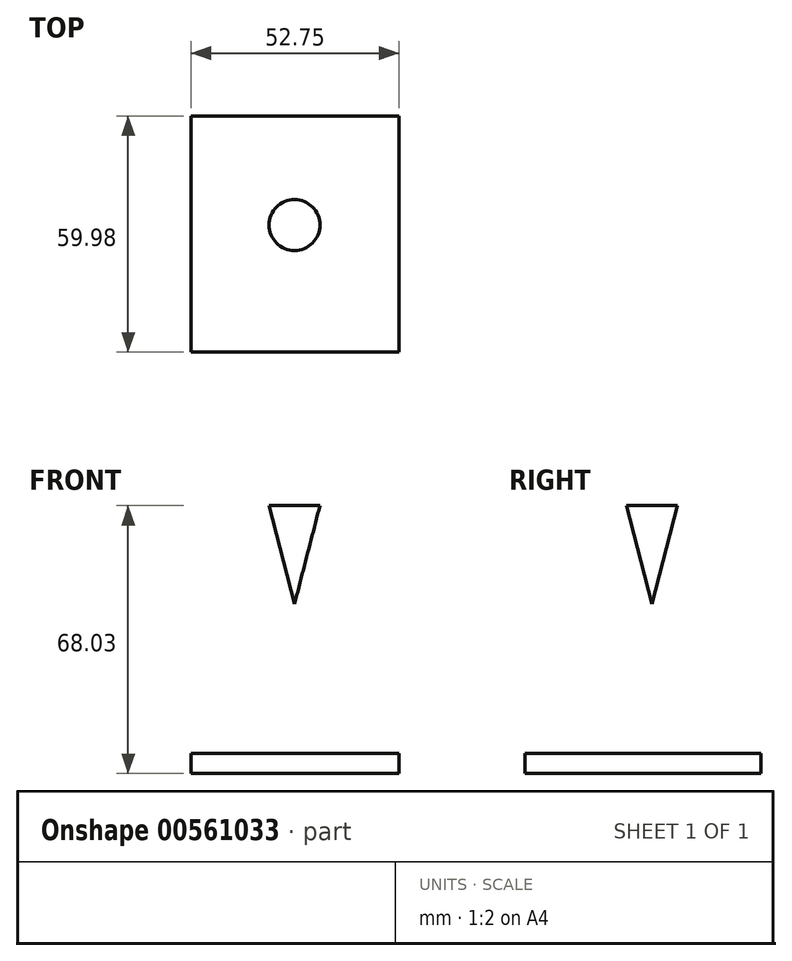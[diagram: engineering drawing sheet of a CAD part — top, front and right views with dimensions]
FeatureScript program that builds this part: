
annotation { "Feature Type Name" : "Feature", "Feature Type Description" : "" }
export const myFeature = defineFeature(function(context is Context, id is Id, definition is map)
    precondition{}
    {
        {
            var Q0;
            Q0=qCreatedBy(makeId("Front.planeOp"),FACE);
            var sketch = newSketch(context, id + "F0", { "sketchPlane" : qUnion([Q0])});
            skLineSegment(sketch, "E0", {"start": v(0, 0) * mm, "end": v(0, 25) * mm});
            skLineSegment(sketch, "E1", {"start": v(0, 25) * mm, "end": v(6.47, 25) * mm});
            skLineSegment(sketch, "E2", {"start": v(6.47, 25) * mm, "end": v(0, 0) * mm});
            skLineSegment(sketch, "E3", {"start": v(0, -37.95) * mm, "end": v(16.47, -37.95) * mm});
            skLineSegment(sketch, "E4", {"start": v(16.47, -37.95) * mm, "end": v(16.47, -42.95) * mm});
            skLineSegment(sketch, "E5", {"start": v(16.47, -42.95) * mm, "end": v(0, -42.95) * mm});
            skLineSegment(sketch, "E6", {"start": v(0, -42.95) * mm, "end": v(0, -37.95) * mm});
            skSolve(sketch);
        }
        {
            var Q0;
            Q0 = qSketchRegion(id + "F0", true);
            var Q1;
            Q1=sQuery(id+"F0.wireOp",EDGE,"E0");
            revolve(context, id + "F1", {"entities" : qUnion([Q0]), "axis" : qUnion([Q1]), "revolveType" : RevolveType.FULL});
        }
        {
            var Q0;
            Q0=qCreatedBy(makeId("Front.planeOp"),FACE);
            var sketch = newSketch(context, id + "F2", { "sketchPlane" : qUnion([Q0])});
            skArc(sketch, "E7", {"start": v(0, -13.15) * mm, "mid": v(13.15, 0) * mm, "end": v(0, 13.15) * mm});
            skLineSegment(sketch, "E8", {"start": v(0, 0) * mm, "end": v(0, -13.15) * mm});
            skLineSegment(sketch, "E9", {"start": v(0, 0) * mm, "end": v(0, 13.15) * mm});
            skSolve(sketch);
        }
        {
            var Q0;
            Q0=makeQuery(id+"F1.opRevolve","SWEPT_FACE",FACE,{"disambiguationData":[OSD([sQuery(id+"F0.wireOp",EDGE,"E3")])]});
            var sketch = newSketch(context, id + "F3", { "sketchPlane" : qUnion([Q0])});
            skLineSegment(sketch, "E10.bottom", {"start": v(-26.22, 27.67) * mm, "end": v(26.53, 27.67) * mm});
            skLineSegment(sketch, "E10.top", {"start": v(-26.22, -32.3) * mm, "end": v(26.53, -32.3) * mm});
            skLineSegment(sketch, "E10.left", {"start": v(-26.22, 27.67) * mm, "end": v(-26.22, -32.3) * mm});
            skLineSegment(sketch, "E10.right", {"start": v(26.53, 27.67) * mm, "end": v(26.53, -32.3) * mm});
            skSolve(sketch);
        }
        {
            var Q0;
            Q0 = qSketchRegion(id + "F3", true);
            extrude(context, id + "F4", {"entities" : qUnion([Q0]), "operationType" : NewBodyOperationType.ADD, "oppositeDirection" : true, "depth" : 5.08 * mm, "offsetDistance" : 25.4 * mm});
        }
    });
